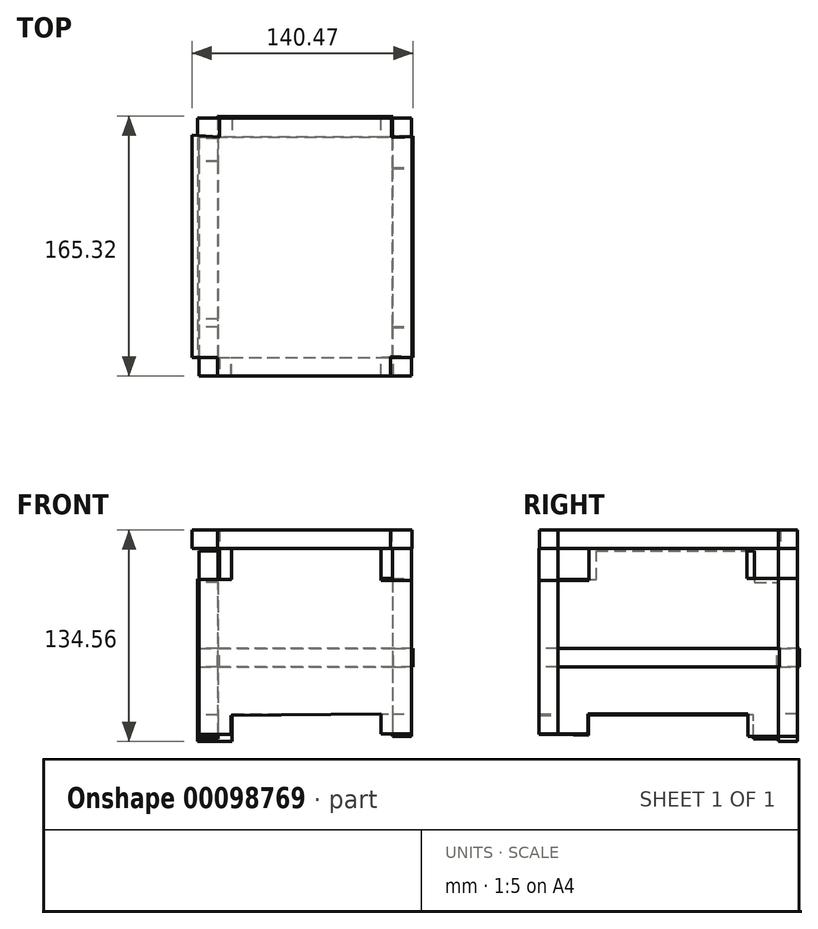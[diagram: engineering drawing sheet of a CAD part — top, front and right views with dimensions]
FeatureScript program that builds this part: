
annotation { "Feature Type Name" : "Feature", "Feature Type Description" : "" }
export const myFeature = defineFeature(function(context is Context, id is Id, definition is map)
    precondition{}
    {
        {
            var Q0;
            Q0=qCreatedBy(makeId("Front.planeOp"),FACE);
            var sketch = newSketch(context, id + "F0", { "sketchPlane" : qUnion([Q0])});
            skLineSegment(sketch, "E0", {"start": v(-40.96, -54.86) * mm, "end": v(-40.96, 43.6) * mm});
            skLineSegment(sketch, "E1", {"start": v(-40.96, 43.6) * mm, "end": v(-20.38, 43.6) * mm});
            skLineSegment(sketch, "E2", {"start": v(-20.38, 43.6) * mm, "end": v(-20.38, 63.37) * mm});
            skLineSegment(sketch, "E3", {"start": v(-20.38, 63.37) * mm, "end": v(74.6, 63.37) * mm});
            skLineSegment(sketch, "E4", {"start": v(74.6, 43.04) * mm, "end": v(74.6, 63.37) * mm});
            skLineSegment(sketch, "E5", {"start": v(74.6, 43.04) * mm, "end": v(93.83, 43.04) * mm});
            skLineSegment(sketch, "E6", {"start": v(93.83, 43.04) * mm, "end": v(93.83, -54.56) * mm});
            skLineSegment(sketch, "E7", {"start": v(93.83, -54.56) * mm, "end": v(74.5, -54.56) * mm});
            skLineSegment(sketch, "E8", {"start": v(-40.96, -54.86) * mm, "end": v(-20.66, -54.86) * mm});
            skLineSegment(sketch, "E9", {"start": v(-20.66, -54.86) * mm, "end": v(-20.66, -42.76) * mm});
            skLineSegment(sketch, "E10", {"start": v(74.5, -54.56) * mm, "end": v(74.5, -41.79) * mm});
            skLineSegment(sketch, "E11", {"start": v(-20.66, -42.76) * mm, "end": v(74.5, -41.79) * mm});
            skSolve(sketch);
        }
        {
            var Q0;
            Q0=makeQuery(id+"F0.imprint","IMPRINT",FACE,{"disambiguationData":[TD([[makeQuery(id+"F0.imprint","IMPRINT",EDGE,{"derivedFrom":sQuery(id+"F0.wireOp",EDGE,"E0")}),-1.0]])]});
            extrude(context, id + "F1", {"entities" : qUnion([Q0]), "depth" : 12 * mm});
        }
        {
            var Q0;
            Q0=makeQuery(id+"F1.opExtrude","SWEPT_FACE",FACE,{"disambiguationData":[OSD([sQuery(id+"F0.wireOp",EDGE,"E6")])]});
            var sketch = newSketch(context, id + "F2", { "sketchPlane" : qUnion([Q0])});
            skLineSegment(sketch, "E12", {"start": v(0, 43.04) * mm, "end": v(19.5, 43.04) * mm});
            skLineSegment(sketch, "E13", {"start": v(19.5, 43.04) * mm, "end": v(19.5, 63.86) * mm});
            skLineSegment(sketch, "E14", {"start": v(19.5, 63.86) * mm, "end": v(119.9, 63.86) * mm});
            skLineSegment(sketch, "E15", {"start": v(119.9, 63.86) * mm, "end": v(119.9, 44.24) * mm});
            skLineSegment(sketch, "E16", {"start": v(119.9, 44.24) * mm, "end": v(139.9, 44.24) * mm});
            skLineSegment(sketch, "E17", {"start": v(139.9, 44.24) * mm, "end": v(139.9, -56.04) * mm});
            skLineSegment(sketch, "E18", {"start": v(139.9, -56.04) * mm, "end": v(120.66, -56.04) * mm});
            skLineSegment(sketch, "E19", {"start": v(120.66, -56.04) * mm, "end": v(120.66, -41.87) * mm});
            skLineSegment(sketch, "E20", {"start": v(120.66, -41.87) * mm, "end": v(18.98, -41.87) * mm});
            skLineSegment(sketch, "E21", {"start": v(18.98, -41.87) * mm, "end": v(18.98, -54.56) * mm});
            skLineSegment(sketch, "E22", {"start": v(18.98, -54.56) * mm, "end": v(0, -54.56) * mm});
            skLineSegment(sketch, "E23", {"start": v(0, -54.56) * mm, "end": v(0, 43.04) * mm});
            skSolve(sketch);
        }
        {
            var Q0;
            Q0=makeQuery(id+"F2.imprint","IMPRINT",FACE,{"disambiguationData":[TD([[makeQuery(id+"F2.imprint","IMPRINT",EDGE,{"derivedFrom":sQuery(id+"F2.wireOp",EDGE,"E12")}),-1.0]])]});
            extrude(context, id + "F3", {"entities" : qUnion([Q0]), "oppositeDirection" : true, "depth" : 12 * mm});
        }
        {
            var Q0;
            Q0=makeQuery(id+"F1.opExtrude","SWEPT_FACE",FACE,{"disambiguationData":[OSD([sQuery(id+"F0.wireOp",EDGE,"E0")])]});
            var sketch = newSketch(context, id + "F4", { "sketchPlane" : qUnion([Q0])});
            skLineSegment(sketch, "E24", {"start": v(0, 43.6) * mm, "end": v(-24.3, 43.6) * mm});
            skLineSegment(sketch, "E25", {"start": v(-24.3, 43.6) * mm, "end": v(-24.3, 61.79) * mm});
            skLineSegment(sketch, "E26", {"start": v(-24.3, 61.79) * mm, "end": v(-124.77, 61.79) * mm});
            skLineSegment(sketch, "E27", {"start": v(-124.77, 61.79) * mm, "end": v(-124.77, 41.72) * mm});
            skLineSegment(sketch, "E28", {"start": v(-124.77, 41.72) * mm, "end": v(-145.47, 41.72) * mm});
            skLineSegment(sketch, "E29", {"start": v(-145.47, 41.72) * mm, "end": v(-145.47, -57.51) * mm});
            skLineSegment(sketch, "E30", {"start": v(-145.47, -57.51) * mm, "end": v(-124.21, -57.51) * mm});
            skLineSegment(sketch, "E31", {"start": v(-124.21, -57.51) * mm, "end": v(-124.21, -42.45) * mm});
            skLineSegment(sketch, "E32", {"start": v(-124.21, -42.45) * mm, "end": v(-19.37, -42.45) * mm});
            skLineSegment(sketch, "E33", {"start": v(-19.37, -42.45) * mm, "end": v(-19.37, -55.45) * mm});
            skLineSegment(sketch, "E34", {"start": v(-19.37, -55.45) * mm, "end": v(0, -54.86) * mm});
            skLineSegment(sketch, "E35", {"start": v(0, -54.86) * mm, "end": v(0, 43.6) * mm});
            skSolve(sketch);
        }
        {
            var Q0;
            Q0=makeQuery(id+"F4.imprint","IMPRINT",FACE,{"disambiguationData":[TD([[makeQuery(id+"F4.imprint","IMPRINT",EDGE,{"derivedFrom":sQuery(id+"F4.wireOp",EDGE,"E24")}),1.0]])]});
            extrude(context, id + "F5", {"entities" : qUnion([Q0]), "oppositeDirection" : true, "depth" : 12 * mm});
        }
        {
            var Q0;
            Q0=makeQuery(id+"F0.imprint","IMPRINT",FACE,{"disambiguationData":[TD([[makeQuery(id+"F0.imprint","IMPRINT",EDGE,{"derivedFrom":sQuery(id+"F0.wireOp",EDGE,"E0")}),-1.0]])]});
            extrude(context, id + "F6", {"entities" : qUnion([Q0]), "depth" : 12 * mm});
        }
        {
            var Q0;
            Q0=makeQuery(id+"F3.opExtrude","SWEPT_FACE",FACE,{"disambiguationData":[OSD([sQuery(id+"F2.wireOp",EDGE,"E17")])]});
            var sketch = newSketch(context, id + "F7", { "sketchPlane" : qUnion([Q0])});
            skLineSegment(sketch, "E36", {"start": v(-93.83, 44.24) * mm, "end": v(-74.2, 44.24) * mm});
            skLineSegment(sketch, "E37", {"start": v(-74.2, 44.24) * mm, "end": v(-74.2, 63.27) * mm});
            skLineSegment(sketch, "E38", {"start": v(-74.2, 63.27) * mm, "end": v(27.97, 63.27) * mm});
            skLineSegment(sketch, "E39", {"start": v(27.97, 63.27) * mm, "end": v(27.97, 44.07) * mm});
            skLineSegment(sketch, "E40", {"start": v(27.97, 44.07) * mm, "end": v(41.85, 44.07) * mm});
            skLineSegment(sketch, "E41", {"start": v(41.85, 44.07) * mm, "end": v(41.85, -59.29) * mm});
            skLineSegment(sketch, "E42", {"start": v(41.85, -59.29) * mm, "end": v(20, -59.29) * mm});
            skLineSegment(sketch, "E43", {"start": v(20, -59.29) * mm, "end": v(20, -41.57) * mm});
            skLineSegment(sketch, "E44", {"start": v(20, -41.57) * mm, "end": v(-81.83, -41.57) * mm});
            skLineSegment(sketch, "E45", {"start": v(-93.83, -56.04) * mm, "end": v(-93.83, 44.24) * mm});
            skLineSegment(sketch, "E46", {"start": v(-81.83, -41.57) * mm, "end": v(-81.83, -56.04) * mm});
            skLineSegment(sketch, "E47", {"start": v(-81.83, -56.04) * mm, "end": v(-93.83, -56.04) * mm});
            skSolve(sketch);
        }
        {
            var Q0;
            {var subQ3=sQuery(id+"F7.wireOp",EDGE,"E37");Q0=makeQuery(id+"F7.imprint","IMPRINT",FACE,{"disambiguationData":[TD([[makeQuery(id+"F7.imprint","IMPRINT",EDGE,{"derivedFrom":subQ3}),-1.0]])]});}
            extrude(context, id + "F8", {"entities" : qUnion([Q0]), "operationType" : NewBodyOperationType.ADD, "depth" : 12 * mm});
        }
        {
            var Q0;
            {var subQ1=sQuery(id+"F7.wireOp",EDGE,"E45");Q0=makeQuery(id+"F7.imprint","IMPRINT",FACE,{"disambiguationData":[TD([[makeQuery(id+"F7.imprint","IMPRINT",EDGE,{"derivedFrom":subQ1}),1.0]])]});}
            extrude(context, id + "F9", {"entities" : qUnion([Q0]), "depth" : 12 * mm});
        }
        {
            var Q0;
            Q0=qCreatedBy(makeId("Top.planeOp"),FACE);
            var sketch = newSketch(context, id + "F10", { "sketchPlane" : qUnion([Q0])});
            skLineSegment(sketch, "E48", {"start": v(-29.12, 153.32) * mm, "end": v(-29.12, 139.09) * mm});
            skLineSegment(sketch, "E49", {"start": v(-29.12, 139.09) * mm, "end": v(-41.83, 139.09) * mm});
            skLineSegment(sketch, "E50", {"start": v(-41.83, 139.09) * mm, "end": v(-41.83, 0) * mm});
            skLineSegment(sketch, "E51", {"start": v(-41.83, 0) * mm, "end": v(-28.1, 0) * mm});
            skLineSegment(sketch, "E52", {"start": v(-28.1, 0) * mm, "end": v(-28.1, -11.76) * mm});
            skLineSegment(sketch, "E53", {"start": v(-28.1, -11.76) * mm, "end": v(82.64, -11.76) * mm});
            skLineSegment(sketch, "E54", {"start": v(82.64, -11.76) * mm, "end": v(82.64, 0) * mm});
            skLineSegment(sketch, "E55", {"start": v(82.64, 0) * mm, "end": v(95.03, 0) * mm});
            skLineSegment(sketch, "E56", {"start": v(95.03, 140.48) * mm, "end": v(82.21, 140.48) * mm});
            skLineSegment(sketch, "E57", {"start": v(82.21, 140.48) * mm, "end": v(82.21, 153.05) * mm});
            skLineSegment(sketch, "E58", {"start": v(82.21, 153.05) * mm, "end": v(-29.12, 153.32) * mm});
            skLineSegment(sketch, "E59", {"start": v(95.03, 140.48) * mm, "end": v(95.03, 0) * mm});
            skSolve(sketch);
        }
        {
            var Q0;
            Q0=makeQuery(id+"F10.imprint","IMPRINT",FACE,{"disambiguationData":[TD([[makeQuery(id+"F10.imprint","IMPRINT",EDGE,{"derivedFrom":sQuery(id+"F10.wireOp",EDGE,"E48")}),1.0]])]});
            extrude(context, id + "F11", {"entities" : qUnion([Q0]), "oppositeDirection" : true, "depth" : 12 * mm});
        }
        {
            var Q0;
            Q0=makeQuery(id+"F8.opExtrude","SWEPT_FACE",FACE,{"disambiguationData":[OSD([sQuery(id+"F7.wireOp",EDGE,"E38")])]});
            var sketch = newSketch(context, id + "F12", { "sketchPlane" : qUnion([Q0])});
            skLineSegment(sketch, "E60", {"start": v(-27.97, 139.9) * mm, "end": v(-27.97, 151.9) * mm});
            skLineSegment(sketch, "E61", {"start": v(-27.97, 151.9) * mm, "end": v(81.18, 151.9) * mm});
            skLineSegment(sketch, "E62", {"start": v(81.18, 151.9) * mm, "end": v(81.18, 139.6) * mm});
            skLineSegment(sketch, "E63", {"start": v(81.18, 139.6) * mm, "end": v(94.4, 140.1) * mm});
            skLineSegment(sketch, "E64", {"start": v(94.4, 140.1) * mm, "end": v(94.4, 0) * mm});
            skLineSegment(sketch, "E65", {"start": v(94.4, 0) * mm, "end": v(80.67, 0.36) * mm});
            skLineSegment(sketch, "E66", {"start": v(80.67, 0.36) * mm, "end": v(80.67, -11.83) * mm});
            skLineSegment(sketch, "E67", {"start": v(80.67, -11.83) * mm, "end": v(-29.17, -11.83) * mm});
            skLineSegment(sketch, "E68", {"start": v(-29.17, -11.83) * mm, "end": v(-29.17, 0) * mm});
            skLineSegment(sketch, "E69", {"start": v(-29.17, 0) * mm, "end": v(-45.44, 0) * mm});
            skLineSegment(sketch, "E70", {"start": v(-45.44, 0) * mm, "end": v(-45.44, 141.12) * mm});
            skLineSegment(sketch, "E71", {"start": v(-45.44, 141.12) * mm, "end": v(-27.97, 139.9) * mm});
            skSolve(sketch);
        }
        {
            var Q0;
            {var subQ3=sQuery(id+"F12.wireOp",EDGE,"E62");Q0=makeQuery(id+"F12.imprint","IMPRINT",FACE,{"disambiguationData":[TD([[makeQuery(id+"F12.imprint","IMPRINT",EDGE,{"derivedFrom":subQ3}),-1.0]])]});}
            var Q1;
            {var subQ0=sQuery(id+"F12.wireOp",EDGE,"E60");Q1=makeQuery(id+"F12.imprint","IMPRINT",FACE,{"disambiguationData":[TD([[makeQuery(id+"F12.imprint","IMPRINT",EDGE,{"derivedFrom":subQ0}),1.0]])]});}
            extrude(context, id + "F13", {"entities" : qUnion([Q0, Q1]), "depth" : 12 * mm});
        }
    });
